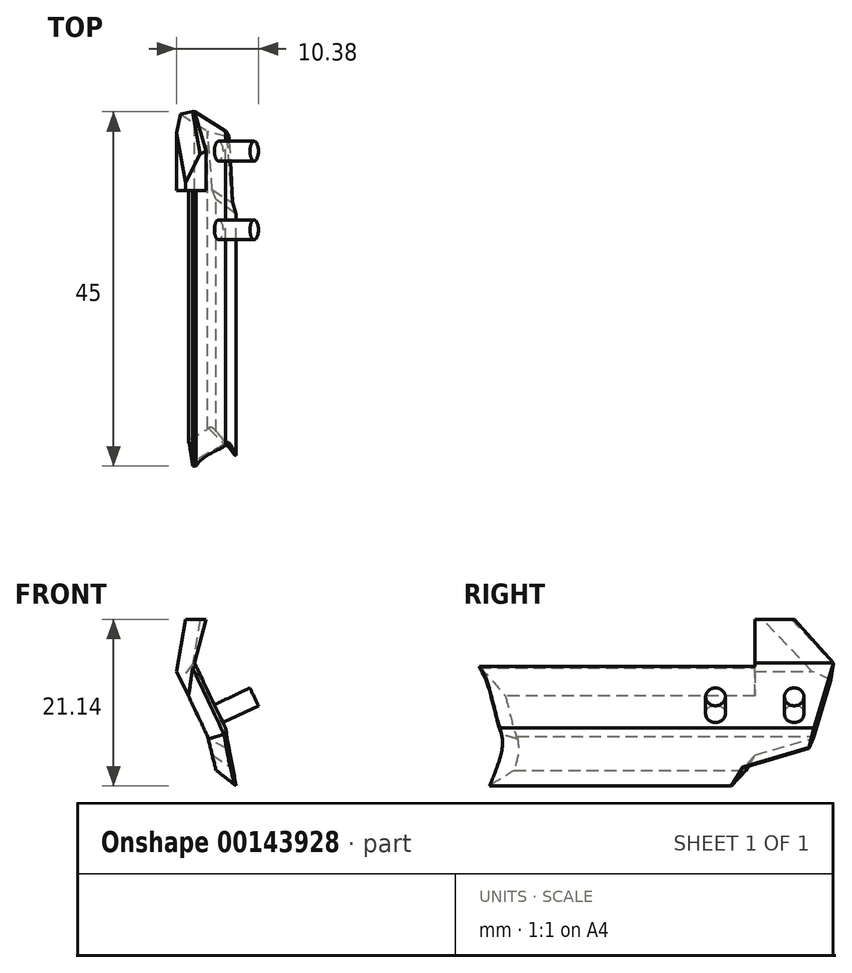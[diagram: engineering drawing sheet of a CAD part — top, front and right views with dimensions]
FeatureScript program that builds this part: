
annotation { "Feature Type Name" : "Feature", "Feature Type Description" : "" }
export const myFeature = defineFeature(function(context is Context, id is Id, definition is map)
    precondition{}
    {
        {
            var Q0;
            Q0=qCreatedBy(makeId("Front.planeOp"),FACE);
            var sketch = newSketch(context, id + "F0", { "sketchPlane" : qUnion([Q0])});
            skLineSegment(sketch, "E0", {"start": v(10.5, 26.96) * mm, "end": v(14.43, 35.23) * mm});
            skLineSegment(sketch, "E1", {"start": v(16.69, 34.16) * mm, "end": v(12.77, 25.9) * mm});
            skLineSegment(sketch, "E2", {"start": v(10.5, 26.96) * mm, "end": v(8.97, 18.68) * mm});
            skLineSegment(sketch, "E3", {"start": v(8.97, 18.68) * mm, "end": v(10.97, 18.68) * mm});
            skLineSegment(sketch, "E4", {"start": v(10.97, 18.68) * mm, "end": v(12.77, 25.9) * mm});
            skLineSegment(sketch, "E5", {"start": v(16.69, 34.16) * mm, "end": v(15.56, 40.74) * mm});
            skPoint(sketch, "E5.endSnap0", {"position": v(15.56, 34.7) * mm});
            skLineSegment(sketch, "E6", {"start": v(15.56, 40.74) * mm, "end": v(12.94, 40.74) * mm});
            skLineSegment(sketch, "E7", {"start": v(12.94, 40.74) * mm, "end": v(14.43, 35.23) * mm});
            skSolve(sketch);
        }
        {
            var Q0;
            Q0=makeQuery(id+"F0.imprint","IMPRINT",FACE,{"disambiguationData":[TD([[makeQuery(id+"F0.imprint","IMPRINT",EDGE,{"derivedFrom":sQuery(id+"F0.wireOp",EDGE,"E0")}),-1.0]])]});
            extrude(context, id + "F1", {"entities" : qUnion([Q0]), "depth" : 45 * mm});
        }
        {
            var Q0;
            Q0=makeQuery(id+"F1.opExtrude","SWEPT_FACE",FACE,{"disambiguationData":[OSD([sQuery(id+"F0.wireOp",EDGE,"E1")])]});
            var sketch = newSketch(context, id + "F2", { "sketchPlane" : qUnion([Q0])});
            skLineSegment(sketch, "E8", {"start": v(-10, 44.01) * mm, "end": v(-10, 37.51) * mm});
            skLineSegment(sketch, "E9", {"start": v(-10, 37.51) * mm, "end": v(-47.68, 37.51) * mm});
            skLineSegment(sketch, "E10", {"start": v(-47.68, 37.51) * mm, "end": v(-47.68, 45.38) * mm});
            skLineSegment(sketch, "E11", {"start": v(-47.68, 45.38) * mm, "end": v(-10, 44.01) * mm});
            skSolve(sketch);
        }
        {
            var Q0;
            Q0=qSketchRegion(id+"F2",true);
            extrude(context, id + "F3", {"entities" : qUnion([Q0]), "operationType" : NewBodyOperationType.REMOVE, "oppositeDirection" : true, "depth" : 25 * mm, "symmetric" : true});
        }
        {
            var Q0;
            Q0=makeQuery(id+"F3.boolean.opBoolean","COPY",EDGE,{"derivedFrom":makeQuery(id+"F3.opExtrude","SWEPT_EDGE",EDGE,{"disambiguationData":[OSD([sQuery(id+"F0.wireOp",EDGE,"I9DD8Fa4-NaBL-5nGr-AlWa-AAlXh3cZLOTC"),sQuery(id+"F0.wireOp",EDGE,"E1"),sQuery(id+"F2.wireOp",EDGE,"E8"),sQuery(id+"F2.wireOp",EDGE,"E11")])]})});
            var Q1;
            Q1=makeQuery(id+"F3.boolean.opBoolean","INTERSECT",EDGE,{"derivedFrom":[makeQuery(id+"F1.opExtrude","SWEPT_FACE",FACE,{"disambiguationData":[OSD([sQuery(id+"F0.wireOp",EDGE,"E1")])]}),makeQuery(id+"F3.opExtrude","SWEPT_FACE",FACE,{"disambiguationData":[OSD([sQuery(id+"F2.wireOp",EDGE,"E9")])]})]});
            chamfer(context, id + "F4", {"entities" : qUnion([Q0, Q1]), "chamferType" : ChamferType.TWO_OFFSETS, "width1" : 3 * mm, "oppositeDirection" : false, "width2" : 2 * mm, "tangentPropagation" : true});
        }
        {
            var Q0;
            Q0=makeQuery(id+"F1.opExtrude","SWEPT_FACE",FACE,{"disambiguationData":[OSD([sQuery(id+"F0.wireOp",EDGE,"E1")])]});
            var sketch = newSketch(context, id + "F5", { "sketchPlane" : qUnion([Q0])});
            skLineSegment(sketch, "E12", {"start": v(0, 38.01) * mm, "end": v(-3.14, 26.42) * mm});
            skLineSegment(sketch, "E13", {"start": v(-3.14, 26.42) * mm, "end": v(-11.5, 23.97) * mm});
            skLineSegment(sketch, "E14", {"start": v(-11.5, 23.97) * mm, "end": v(-15.54, 17.62) * mm});
            skLineSegment(sketch, "E15", {"start": v(-15.54, 17.62) * mm, "end": v(1.69, 17.62) * mm});
            skLineSegment(sketch, "E16", {"start": v(1.69, 17.62) * mm, "end": v(2.2, 38.01) * mm});
            skFitSpline(sketch, "E17", {"points": [v(-45, 37.51) * mm, v(-42.65, 29.8) * mm, v(-42.07, 26.42) * mm, v(-45, 18.78) * mm], "startDerivative": vector(9.01, -10.7) * mm, "endDerivative": vector(-9.27, -19.6) * mm});
            skLineSegment(sketch, "E18", {"start": v(-45, 37.51) * mm, "end": v(-47.05, 37.51) * mm});
            skLineSegment(sketch, "E19", {"start": v(-47.05, 37.51) * mm, "end": v(-45, 18.78) * mm});
            skLineSegment(sketch, "E20", {"start": v(0, 38.01) * mm, "end": v(-7.62, 44.68) * mm});
            skLineSegment(sketch, "E21", {"start": v(-7.62, 44.68) * mm, "end": v(2.2, 44.68) * mm});
            skLineSegment(sketch, "E22", {"start": v(2.2, 44.68) * mm, "end": v(2.2, 38.01) * mm});
            skSolve(sketch);
        }
        {
            var Q0;
            Q0=qSketchRegion(id+"F5",true);
            extrude(context, id + "F6", {"entities" : qUnion([Q0]), "operationType" : NewBodyOperationType.REMOVE, "oppositeDirection" : true, "depth" : 25 * mm, "symmetric" : true});
        }
        {
            var Q0;
            Q0=makeQuery(id+"F6.boolean.opBoolean","INTERSECT",EDGE,{"derivedFrom":[makeQuery(id+"F1.opExtrude","SWEPT_FACE",FACE,{"disambiguationData":[OSD([sQuery(id+"F0.wireOp",EDGE,"E5")])]}),makeQuery(id+"F6.opExtrude","SWEPT_FACE",FACE,{"disambiguationData":[OSD([sQuery(id+"F5.wireOp",EDGE,"E20")])]})]});
            chamfer(context, id + "F7", {"entities" : qUnion([Q0]), "width" : 2 * mm, "tangentPropagation" : true});
        }
        {
            var Q0;
            Q0=makeQuery(id+"F6.boolean.opBoolean","INTERSECT",EDGE,{"derivedFrom":[makeQuery(id+"F1.opExtrude","SWEPT_FACE",FACE,{"disambiguationData":[OSD([sQuery(id+"F0.wireOp",EDGE,"E1")])]}),makeQuery(id+"F6.opExtrude","SWEPT_FACE",FACE,{"disambiguationData":[OSD([sQuery(id+"F5.wireOp",EDGE,"E17")])]})]});
            var Q1;
            Q1=makeQuery(id+"F6.boolean.opBoolean","INTERSECT",EDGE,{"derivedFrom":[makeQuery(id+"F1.opExtrude","SWEPT_FACE",FACE,{"disambiguationData":[OSD([sQuery(id+"F0.wireOp",EDGE,"E4")])]}),makeQuery(id+"F6.opExtrude","SWEPT_FACE",FACE,{"disambiguationData":[OSD([sQuery(id+"F5.wireOp",EDGE,"E17")])]})]});
            chamfer(context, id + "F8", {"entities" : qUnion([Q0, Q1]), "width" : 2 * mm, "tangentPropagation" : true});
        }
        {
            var Q0;
            Q0=makeQuery(id+"F1.opExtrude","SWEPT_FACE",FACE,{"disambiguationData":[OSD([sQuery(id+"F0.wireOp",EDGE,"E0")])]});
            var sketch = newSketch(context, id + "F9", { "sketchPlane" : qUnion([Q0])});
            skCircle(sketch, "E23", {"center": v(5, 30.86) * mm, "radius": 1.25 * mm});
            skCircle(sketch, "E24", {"center": v(15, 30.86) * mm, "radius": 1.25 * mm});
            skSolve(sketch);
        }
        {
            var Q0;
            Q0=qSketchRegion(id+"F9",true);
            extrude(context, id + "F10", {"entities" : qUnion([Q0]), "operationType" : NewBodyOperationType.ADD, "depth" : 5 * mm});
        }
        {
            var Q0;
            Q0=makeQuery(id+"F6.boolean.opBoolean","INTERSECT",EDGE,{"derivedFrom":[makeQuery(id+"F1.opExtrude","SWEPT_FACE",FACE,{"disambiguationData":[OSD([sQuery(id+"F0.wireOp",EDGE,"E4")])]}),makeQuery(id+"F6.opExtrude","SWEPT_FACE",FACE,{"disambiguationData":[OSD([sQuery(id+"F5.wireOp",EDGE,"E13")])]})]});
            chamfer(context, id + "F11", {"entities" : qUnion([Q0]), "width" : 2 * mm, "tangentPropagation" : true});
        }
        {
            var Q0;
            Q0=makeQuery(id+"F1.opExtrude","SWEPT_EDGE",EDGE,{"disambiguationData":[OSD([sQuery(id+"F0.wireOp",EDGE,"E3"),sQuery(id+"F0.wireOp",EDGE,"E4")])]});
            chamfer(context, id + "F12", {"entities" : qUnion([Q0]), "width" : 3 * mm, "tangentPropagation" : true});
        }
        {
            var Q0;
            Q0=makeQuery(id+"F1.opExtrude","SWEPT_BODY",BODY,{"disambiguationData":[OSD([sQuery(id+"F0.wireOp",EDGE,"E0"),sQuery(id+"F0.wireOp",EDGE,"E1"),sQuery(id+"F0.wireOp",EDGE,"E2"),sQuery(id+"F0.wireOp",EDGE,"E3"),sQuery(id+"F0.wireOp",EDGE,"E4"),sQuery(id+"F0.wireOp",EDGE,"E5"),sQuery(id+"F0.wireOp",EDGE,"E6"),sQuery(id+"F0.wireOp",EDGE,"E7")])]});
            var Q1;
            Q1=qCreatedBy(makeId("Right.planeOp"),FACE);
            mirror(context, id + "F13", {"entities" : qUnion([Q0]), "mirrorPlane" : qUnion([Q1])});
        }
        {
            var Q0;
            Q0=makeQuery(id+"F1.opExtrude","SWEPT_BODY",BODY,{"disambiguationData":[OSD([sQuery(id+"F0.wireOp",EDGE,"E0"),sQuery(id+"F0.wireOp",EDGE,"E1"),sQuery(id+"F0.wireOp",EDGE,"E2"),sQuery(id+"F0.wireOp",EDGE,"E3"),sQuery(id+"F0.wireOp",EDGE,"E4"),sQuery(id+"F0.wireOp",EDGE,"E5"),sQuery(id+"F0.wireOp",EDGE,"E6"),sQuery(id+"F0.wireOp",EDGE,"E7")])]});
            deleteBodies(context, id + "F14", {"entities" : qUnion([Q0])});
        }
    });
